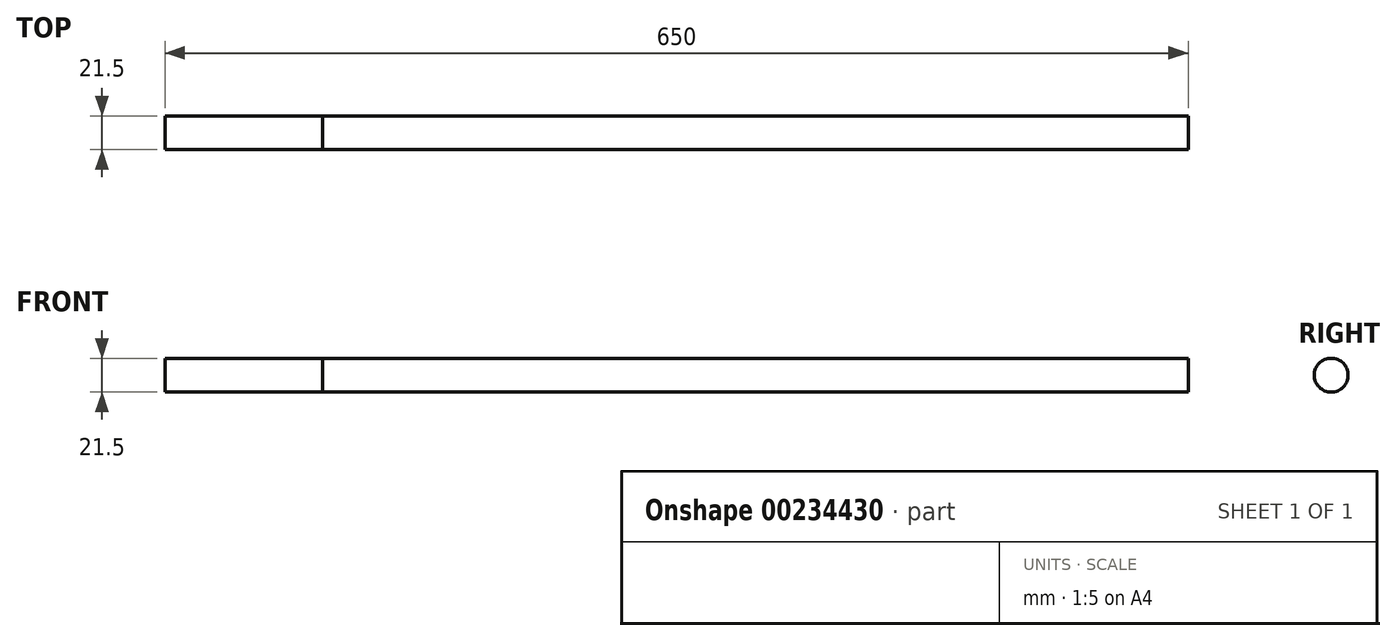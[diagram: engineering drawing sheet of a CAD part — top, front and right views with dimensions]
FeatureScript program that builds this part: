
annotation { "Feature Type Name" : "Feature", "Feature Type Description" : "" }
export const myFeature = defineFeature(function(context is Context, id is Id, definition is map)
    precondition{}
    {
        {
            var Q0;
            Q0=qCreatedBy(makeId("Right.planeOp"),FACE);
            var sketch = newSketch(context, id + "F0", { "sketchPlane" : qUnion([Q0])});
            skCircle(sketch, "E0", {"center": v(0, 0) * mm, "radius": 10.75 * mm});
            skSolve(sketch);
        }
        {
            var Q0;
            Q0=makeQuery(id+"F0.imprint","IMPRINT",FACE,{"disambiguationData":[TD([[makeQuery(id+"F0.imprint","IMPRINT",EDGE,{"derivedFrom":sQuery(id+"F0.wireOp",EDGE,"E0")}),1.0]])]});
            extrude(context, id + "F1", {"entities" : qUnion([Q0]), "depth" : 550 * mm});
        }
        {
            var Q0;
            Q0=makeQuery(id+"F0.imprint","IMPRINT",FACE,{"disambiguationData":[TD([[makeQuery(id+"F0.imprint","IMPRINT",EDGE,{"derivedFrom":sQuery(id+"F0.wireOp",EDGE,"E0")}),1.0]])]});
            var Q1;
            Q1=sQuery(id+"F0.wireOp",EDGE,"E0");
            extrude(context, id + "F2", {"entities" : qUnion([Q0]), "surfaceEntities" : qUnion([Q1]), "oppositeDirection" : true, "depth" : 100 * mm});
        }
    });
